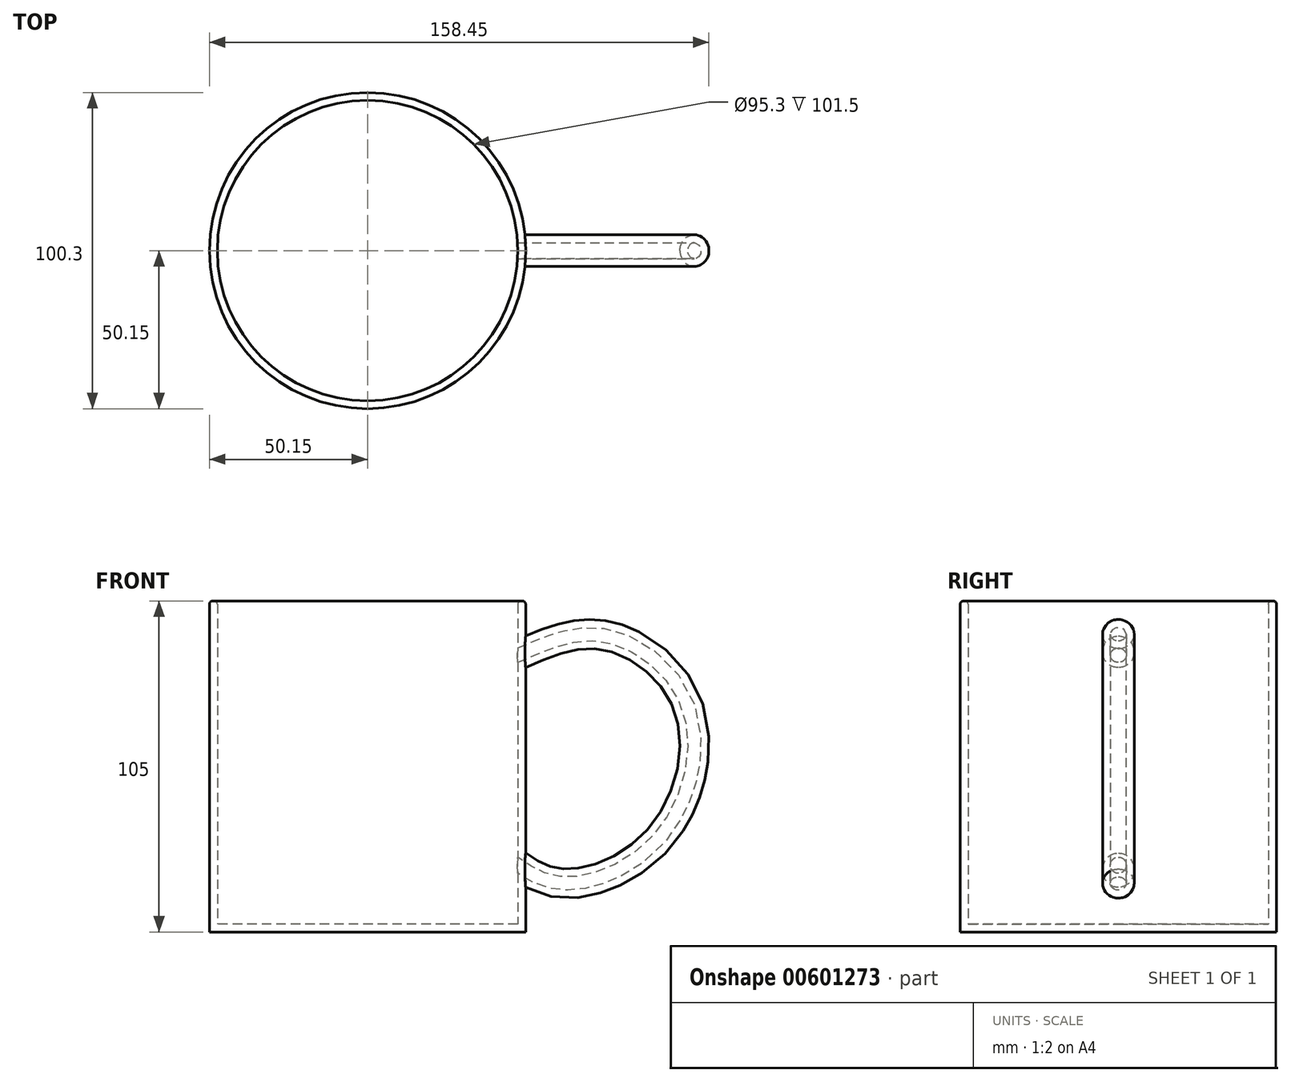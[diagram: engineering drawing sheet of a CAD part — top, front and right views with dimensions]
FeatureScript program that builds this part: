
annotation { "Feature Type Name" : "Feature", "Feature Type Description" : "" }
export const myFeature = defineFeature(function(context is Context, id is Id, definition is map)
    precondition{}
    {
        {
            var Q0;
            Q0=qCreatedBy(makeId("Top.planeOp"),FACE);
            var sketch = newSketch(context, id + "F0", { "sketchPlane" : qUnion([Q0])});
            skCircle(sketch, "E0", {"center": v(0, 0) * mm, "radius": 50.15 * mm});
            skSolve(sketch);
        }
        {
            var Q0;
            Q0 = qSketchRegion(id + "F0", true);
            extrude(context, id + "F1", {"entities" : qUnion([Q0]), "depth" : 105 * mm, "offsetDistance" : 25 * mm});
        }
        {
            var Q0;
            Q0=qCreatedBy(makeId("Right.planeOp"),FACE);
            cPlane(context, id + "F2", {"entities" : qUnion([Q0]), "cplaneType" : CPlaneType.OFFSET, "offset" : 50.15 * mm, "width" : 150 * mm, "height" : 150 * mm});
        }
        {
            var Q0;
            Q0=qCreatedBy(makeId("Front.planeOp"),FACE);
            var sketch = newSketch(context, id + "F3", { "sketchPlane" : qUnion([Q0])});
            skFitSpline(sketch, "E1", {"points": [v(48.1, 87.23) * mm, v(75.3, 93.35) * mm, v(101.13, 70.92) * mm, v(91.95, 30.13) * mm, v(61.7, 16.19) * mm, v(45.38, 23.67) * mm], "startDerivative": vector(138.98, 61.23) * mm, "endDerivative": vector(-93.94, 68.3) * mm});
            skSolve(sketch);
        }
        {
            var Q0;
            Q0=qCreatedBy(id+"F2.planeOp",FACE);
            var sketch = newSketch(context, id + "F4", { "sketchPlane" : qUnion([Q0])});
            skCircle(sketch, "E2", {"center": v(0, 88.9) * mm, "radius": 5.02 * mm});
            skSolve(sketch);
        }
        {
            var Q0;
            Q0=makeQuery(id+"F4.imprint","IMPRINT",FACE,{"disambiguationData":[TD([[makeQuery(id+"F4.imprint","IMPRINT",EDGE,{"derivedFrom":sQuery(id+"F4.wireOp",EDGE,"E2")}),1.0]])]});
            var Q1;
            Q1=sQuery(id+"F3.wireOp",EDGE,"E1");
            sweep(context, id + "F5", {"operationType" : NewBodyOperationType.ADD, "profiles" : qUnion([Q0]), "path" : qUnion([Q1])});
        }
        {
            var Q0;
            Q0=makeQuery(id+"F1.opExtrude","CAP_FACE",FACE,{"disambiguationData":[OSD([sQuery(id+"F0.wireOp",EDGE,"E0")])],"isStart":false});
            shell(context, id + "F6", {"entities" : qUnion([Q0]), "thickness" : 2.5 * mm});
        }
        {
            var Q0;
            Q0=makeQuery(id+"F1.opExtrude","CAP_EDGE",EDGE,{"disambiguationData":[OSD([sQuery(id+"F0.wireOp",EDGE,"E0")])],"isStart":false});
            var Q1;
            {var subQ0=sQuery(id+"F0.wireOp",EDGE,"E0");Q1=makeQuery(id+"F6.opShell","OFFSET_EDGE",EDGE,{"disambiguationData":[OSD([subQ0]),TDD([makeQuery(id+"F1.opExtrude","CAP_EDGE",EDGE,{"disambiguationData":[OSD([subQ0])],"isStart":false})])]});}
            fillet(context, id + "F7", {"entities" : qUnion([Q0, Q1]), "radius" : 1 * mm, "tangentPropagation" : true, "allowEdgeOverflow" : false});
        }
    });
